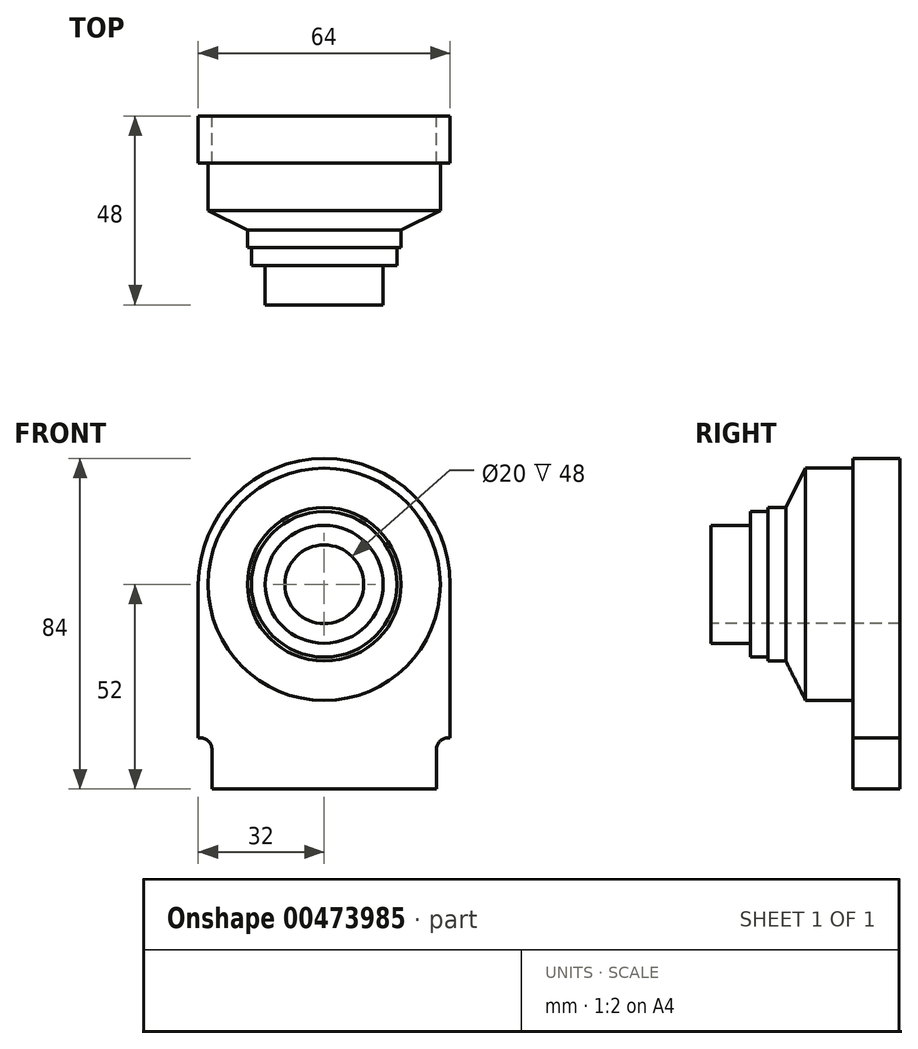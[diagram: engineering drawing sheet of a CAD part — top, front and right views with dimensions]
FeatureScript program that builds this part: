
annotation { "Feature Type Name" : "Feature", "Feature Type Description" : "" }
export const myFeature = defineFeature(function(context is Context, id is Id, definition is map)
    precondition{}
    {
        {
            var Q0;
            Q0=qCreatedBy(makeId("Front.planeOp"),FACE);
            var sketch = newSketch(context, id + "F0", { "sketchPlane" : qUnion([Q0])});
            skArc(sketch, "E0", {"start": v(32, 0) * mm, "mid": v(0, 32) * mm, "end": v(-32, 0) * mm});
            skLineSegment(sketch, "E1.bottom", {"start": v(-32, 0) * mm, "end": v(32, 0) * mm});
            skLineSegment(sketch, "E1.top", {"start": v(-32, -39) * mm, "end": v(-31.5, -39) * mm});
            skLineSegment(sketch, "E1.left", {"start": v(-32, 0) * mm, "end": v(-32, -39) * mm});
            skLineSegment(sketch, "E1.right", {"start": v(32, 0) * mm, "end": v(32, -39) * mm});
            skLineSegment(sketch, "E2.top", {"start": v(-28.5, -52) * mm, "end": v(28.5, -52) * mm});
            skLineSegment(sketch, "E2.left", {"start": v(-28.5, -42) * mm, "end": v(-28.5, -52) * mm});
            skLineSegment(sketch, "E2.right", {"start": v(28.5, -42) * mm, "end": v(28.5, -52) * mm});
            skLineSegment(sketch, "E3.trimOffspring", {"start": v(31.5, -39) * mm, "end": v(32, -39) * mm});
            skPoint(sketch, "E4.visualSharp", {"position": v(-28.5, -39) * mm});
            skArc(sketch, "E4.filletArc", {"start": v(-28.5, -42) * mm, "mid": v(-29.38, -39.88) * mm, "end": v(-31.5, -39) * mm});
            skPoint(sketch, "E5.visualSharp", {"position": v(28.5, -39) * mm});
            skArc(sketch, "E5.filletArc", {"start": v(31.5, -39) * mm, "mid": v(29.38, -39.88) * mm, "end": v(28.5, -42) * mm});
            skSolve(sketch);
        }
        {
            var Q0;
            Q0 = qSketchRegion(id + "F0", true);
            extrude(context, id + "F1", {"entities" : qUnion([Q0]), "depth" : 12 * mm});
        }
        {
            var Q0;
            Q0=makeQuery(id+"F1.opExtrude","CAP_FACE",FACE,{"disambiguationData":[OSD([sQuery(id+"F0.wireOp",EDGE,"E0"),sQuery(id+"F0.wireOp",EDGE,"E1.top"),sQuery(id+"F0.wireOp",EDGE,"E1.left"),sQuery(id+"F0.wireOp",EDGE,"E1.right"),sQuery(id+"F0.wireOp",EDGE,"E2.top"),sQuery(id+"F0.wireOp",EDGE,"E2.left"),sQuery(id+"F0.wireOp",EDGE,"E2.right"),sQuery(id+"F0.wireOp",EDGE,"E3.trimOffspring"),sQuery(id+"F0.wireOp",EDGE,"E4.filletArc"),sQuery(id+"F0.wireOp",EDGE,"E5.filletArc")])],"isStart":false});
            var sketch = newSketch(context, id + "F2", { "sketchPlane" : qUnion([Q0])});
            skCircle(sketch, "E6", {"center": v(0, 0) * mm, "radius": 29.5 * mm});
            skSolve(sketch);
        }
        {
            var Q0;
            Q0=makeQuery(id+"F2.imprint","IMPRINT",FACE,{"disambiguationData":[TD([[makeQuery(id+"F2.imprint","IMPRINT",EDGE,{"derivedFrom":sQuery(id+"F2.wireOp",EDGE,"E6")}),1.0]])]});
            extrude(context, id + "F3", {"entities" : qUnion([Q0]), "operationType" : NewBodyOperationType.ADD, "depth" : 12 * mm});
        }
        {
            var Q0;
            Q0=makeQuery(id+"F3.opExtrude","CAP_FACE",FACE,{"disambiguationData":[OSD([sQuery(id+"F2.wireOp",EDGE,"E6")])],"isStart":false});
            cPlane(context, id + "F4", {"entities" : qUnion([Q0]), "cplaneType" : CPlaneType.OFFSET, "offset" : 5 * mm, "width" : 150 * mm, "height" : 150 * mm});
        }
        {
            var Q0;
            Q0=qCreatedBy(id+"F4.planeOp",FACE);
            var sketch = newSketch(context, id + "F5", { "sketchPlane" : qUnion([Q0])});
            skCircle(sketch, "E7", {"center": v(0, 0) * mm, "radius": 19.5 * mm});
            skSolve(sketch);
        }
        {
            var Q1;
            Q1=makeQuery(id+"F3.opExtrude","CAP_FACE",FACE,{"disambiguationData":[OSD([sQuery(id+"F2.wireOp",EDGE,"E6")])],"isStart":false});
            var Q2;
            Q2=makeQuery(id+"F5.imprint","IMPRINT",FACE,{"disambiguationData":[TD([[makeQuery(id+"F5.imprint","IMPRINT",EDGE,{"derivedFrom":sQuery(id+"F5.wireOp",EDGE,"E7")}),1.0]])]});
            loft(context, id + "F6", {"operationType" : NewBodyOperationType.ADD, "sheetProfilesArray" : [{ "sheetProfileEntities" : qUnion([Q1]) }, { "sheetProfileEntities" : qUnion([Q2]) }]});
        }
        {
            var Q0;
            Q0=makeQuery(id+"F6.opLoft","CAP_FACE",FACE,{"disambiguationData":[OSD([makeQuery(id+"F5.imprint","IMPRINT",FACE,{"disambiguationData":[TD([[makeQuery(id+"F5.imprint","IMPRINT",EDGE,{"derivedFrom":sQuery(id+"F5.wireOp",EDGE,"E7")}),1.0]])]})])],"isStart":true});
            extrude(context, id + "F7", {"entities" : qUnion([Q0]), "operationType" : NewBodyOperationType.ADD, "depth" : 4.5 * mm});
        }
        {
            var Q0;
            Q0=makeQuery(id+"F7.opExtrude","CAP_FACE",FACE,{"disambiguationData":[OSD([makeQuery(id+"F5.imprint","IMPRINT",FACE,{"disambiguationData":[TD([[makeQuery(id+"F5.imprint","IMPRINT",EDGE,{"derivedFrom":sQuery(id+"F5.wireOp",EDGE,"E7")}),1.0]])]})])],"isStart":false});
            var sketch = newSketch(context, id + "F8", { "sketchPlane" : qUnion([Q0])});
            skCircle(sketch, "E8", {"center": v(0, 0) * mm, "radius": 18.5 * mm});
            skSolve(sketch);
        }
        {
            var Q0;
            Q0=makeQuery(id+"F8.imprint","IMPRINT",FACE,{"disambiguationData":[TD([[makeQuery(id+"F8.imprint","IMPRINT",EDGE,{"derivedFrom":sQuery(id+"F8.wireOp",EDGE,"E8")}),1.0]])]});
            extrude(context, id + "F9", {"entities" : qUnion([Q0]), "operationType" : NewBodyOperationType.ADD, "depth" : 4.5 * mm});
        }
        {
            var Q0;
            Q0=makeQuery(id+"F9.opExtrude","CAP_FACE",FACE,{"disambiguationData":[OSD([sQuery(id+"F8.wireOp",EDGE,"E8")])],"isStart":false});
            var sketch = newSketch(context, id + "F10", { "sketchPlane" : qUnion([Q0])});
            skCircle(sketch, "E9", {"center": v(0, 0) * mm, "radius": 15 * mm});
            skSolve(sketch);
        }
        {
            var Q0;
            Q0=makeQuery(id+"F10.imprint","IMPRINT",FACE,{"disambiguationData":[TD([[makeQuery(id+"F10.imprint","IMPRINT",EDGE,{"derivedFrom":sQuery(id+"F10.wireOp",EDGE,"E9")}),1.0]])]});
            extrude(context, id + "F11", {"entities" : qUnion([Q0]), "operationType" : NewBodyOperationType.ADD, "depth" : 10 * mm});
        }
        {
            var Q0;
            Q0=makeQuery(id+"F11.opExtrude","CAP_FACE",FACE,{"disambiguationData":[OSD([sQuery(id+"F10.wireOp",EDGE,"E9")])],"isStart":false});
            var sketch = newSketch(context, id + "F12", { "sketchPlane" : qUnion([Q0])});
            skCircle(sketch, "E10", {"center": v(0, 0) * mm, "radius": 10 * mm});
            skSolve(sketch);
        }
        {
            var Q0;
            Q0=makeQuery(id+"F12.imprint","IMPRINT",FACE,{"disambiguationData":[TD([[makeQuery(id+"F12.imprint","IMPRINT",EDGE,{"derivedFrom":sQuery(id+"F12.wireOp",EDGE,"E10")}),1.0]])]});
            extrude(context, id + "F13", {"entities" : qUnion([Q0]), "operationType" : NewBodyOperationType.REMOVE, "endBound" : BoundingType.THROUGH_ALL, "oppositeDirection" : true, "depth" : 25 * mm});
        }
    });
